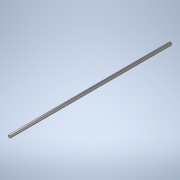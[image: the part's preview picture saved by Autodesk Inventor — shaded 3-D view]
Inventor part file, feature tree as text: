
AUTODESK INVENTOR PART (.ipt)
format: ipt  version: 2020 (Build 240168000, 168)  size: 108,544 bytes
history: native  units: in
note: dims shown in document units (in); Inventor stores cm internally (conversion verified against a paired STEP export)
features: extrude x1, sketch x1
ambient origin geometry x8: Origin, YZ Plane, XZ Plane, XY Plane, X Axis, Y Axis, Z Axis, Center Point
bodies: Solid1 (feature_tree)
feature tree (2):
  extrude  "Extrusion1"  Depth=32.0in TaperAngle=0.0deg
  sketch  "Sketch1"  dims[d0=0.5in d1=32.0in d2=0.0in]
